# Revit family: RL-5 Rücklaufventil DG 3923
name_source: partatom
category: Rohrzubehör
units: mm (PartAtom-declared; Revit-internal decimal feet)

## family parameters
Arbeitsebenenbasiert = Nein
Beim Laden mit Abzugskörper schneiden = Nein
Bemaßung runder Anschluss = Durchmesser verwenden
Gemeinsam genutzt = Nein
Immer vertikal = Nein
OmniClass-Nummer = 23.65.55.14
OmniClass-Titel = Valves for Liquid Services
Teiletyp = Unterbricht

## types (1)
- RL-5 Rücklaufventil DG 3923
    Anwendungsgebiet = Warmwasser-Heizungsanlagen
Durch den Einbau des Rücklaufventils ist der Heizkörper-Rücklaufanschluß absperrbar.
Bei gleichzeitiger Absperrung des Vorlaufventils kann der Heizkörper bei unter Druck stehender Anlage demontiert werden.
Servicearbeiten oder Arbeiten an der Wand hinter dem Heizkörper (Tapezierung, Verfliesung) sind durchführbar, ohne die übrige Anlage stillsetzen zu müssen.
Mit dem HERZ-RL-5-Ventil kann die durch den Heizkörper strömende Wassermenge entsprechend der geforderten Leistung genau einreguliert werden.
Dies empfiehlt sich besonders beim Einbau von Thermostatventilen ohne Voreinstellung, weil durch die Begrenzung der Wassermenge voll wirksam wird und das hydraulische Gleichgewicht der Anlage erhalten bleibt.
Über das HERZ-RL-5-Ventil kann der Heizkörper oder die Anlage gefüllt oder entleert werden.
    Ausführungen = Alle Modelle werden in vernickelter Ausführung geliefert und sind Universalmodelle mit Spezialmuffe für Gewinderohr
und Klemmsetanschluß.
    Gehäuse = vernickeltes Messing
    H03 = 5 mm  [stored 0.0164042 ft]
    H05 = 9.5 mm
    H06 = 3.5 mm  [stored 0.0114829 ft]
    Hersteller = HERZ Armaturen Ges.m.b.H
    Max.Betriebsdruck = 1000000.0 Pa
    Max.Betriebstemperatur = 120 °C
    Medium = Heizwasserqualität entsprechend ÖNORM H 5195 bzw. VDI-Richtllinie 2035.
    R01 = 11 mm  [stored 0.0360892 ft]
    R02 = 9.75 mm  [stored 0.0319882 ft]
    R04 = 12 mm  [stored 0.0393701 ft]
    R05 = 9.75 mm  [stored 0.0319882 ft]
    S01 = 10 mm  [stored 0.0328084 ft]
    S03 = 61 mm
    S04 = 45 mm
    SCRNCODE = 05;01;02
    SCRNSEQ = ARM;ARM_TYP="ALLF";2
    URL = www.herz-armaturen.at
    Vorgabe-Ansicht = 0 mm  [stored 0 ft]
    W01 = 120.00°

note: [stored X ft] marks values corroborated as IEEE doubles in the binary element streams (Revit-internal decimal feet)
